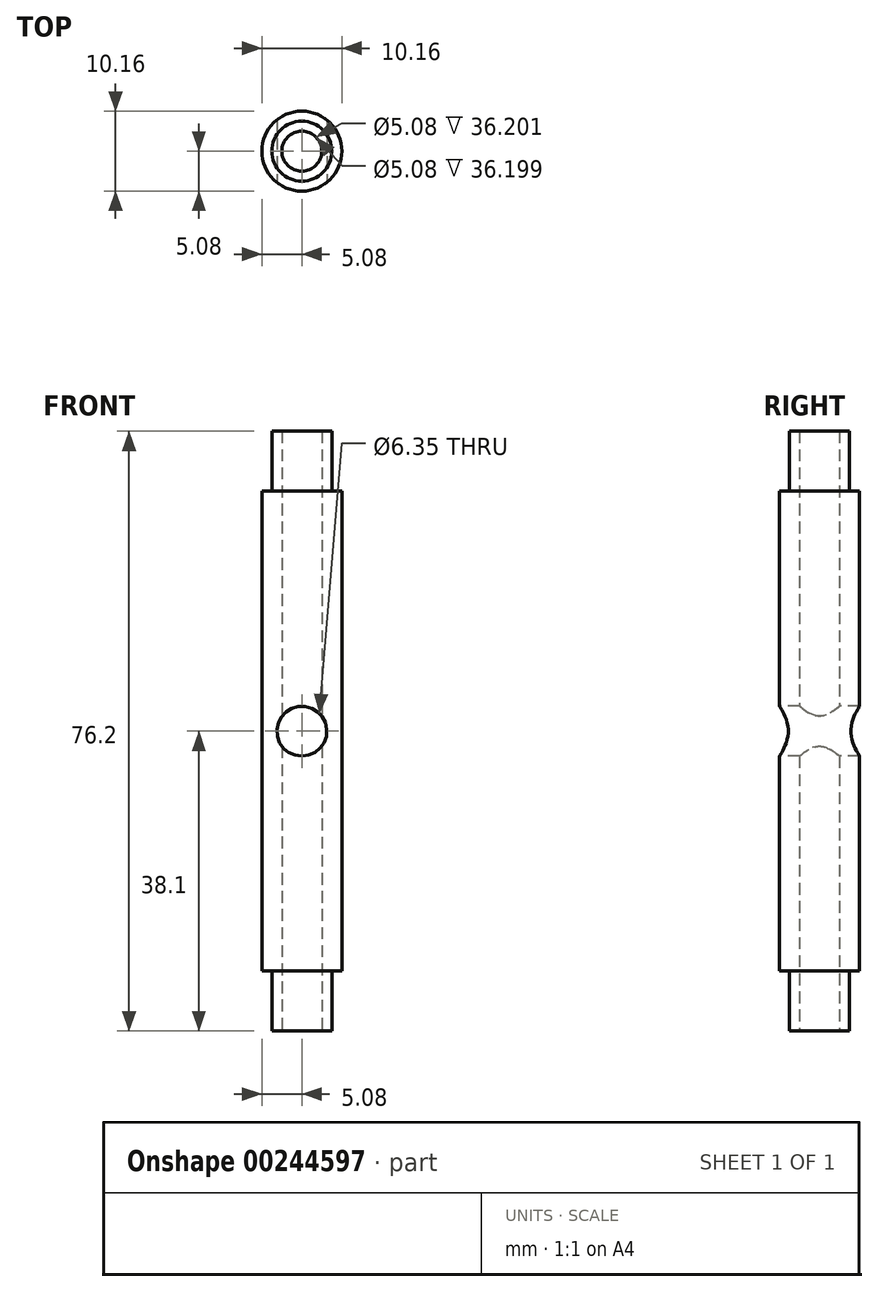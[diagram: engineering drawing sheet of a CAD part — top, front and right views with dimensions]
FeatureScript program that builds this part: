
annotation { "Feature Type Name" : "Feature", "Feature Type Description" : "" }
export const myFeature = defineFeature(function(context is Context, id is Id, definition is map)
    precondition{}
    {
        {
            var Q0;
            Q0=qCreatedBy(makeId("Top.planeOp"),FACE);
            var sketch = newSketch(context, id + "F0", { "sketchPlane" : qUnion([Q0])});
            skCircle(sketch, "E0", {"center": v(0, 0) * mm, "radius": 3.81 * mm});
            skSolve(sketch);
        }
        {
            var Q0;
            Q0 = qSketchRegion(id + "F0", true);
            extrude(context, id + "F1", {"entities" : qUnion([Q0]), "depth" : 7.62 * mm});
        }
        {
            var Q0;
            Q0=makeQuery(id+"F1.opExtrude","CAP_FACE",FACE,{"disambiguationData":[OSD([sQuery(id+"F0.wireOp",EDGE,"E0")])],"isStart":false});
            var sketch = newSketch(context, id + "F2", { "sketchPlane" : qUnion([Q0])});
            skCircle(sketch, "E1", {"center": v(0, 0) * mm, "radius": 5.08 * mm});
            skSolve(sketch);
        }
        {
            var Q0;
            Q0 = qSketchRegion(id + "F2", true);
            extrude(context, id + "F3", {"entities" : qUnion([Q0]), "operationType" : NewBodyOperationType.ADD, "depth" : 60.96 * mm});
        }
        {
            var Q0;
            Q0=makeQuery(id+"F3.opExtrude","CAP_FACE",FACE,{"disambiguationData":[OSD([sQuery(id+"F2.wireOp",EDGE,"E1")])],"isStart":false});
            var sketch = newSketch(context, id + "F4", { "sketchPlane" : qUnion([Q0])});
            skCircle(sketch, "E2", {"center": v(0, 0) * mm, "radius": 3.81 * mm});
            skSolve(sketch);
        }
        {
            var Q0;
            Q0 = qSketchRegion(id + "F4", true);
            extrude(context, id + "F5", {"entities" : qUnion([Q0]), "operationType" : NewBodyOperationType.ADD, "depth" : 7.62 * mm});
        }
        {
            var Q0;
            Q0=qCreatedBy(makeId("Front.planeOp"),FACE);
            var sketch = newSketch(context, id + "F6", { "sketchPlane" : qUnion([Q0])});
            skCircle(sketch, "E3", {"center": v(0, 38.1) * mm, "radius": 3.18 * mm});
            skSolve(sketch);
        }
        {
            var Q0;
            Q0 = qSketchRegion(id + "F6", true);
            extrude(context, id + "F7", {"entities" : qUnion([Q0]), "operationType" : NewBodyOperationType.REMOVE, "oppositeDirection" : true, "depth" : 25.4 * mm, "hasSecondDirection" : true, "secondDirectionOppositeDirection" : false, "secondDirectionDepth" : 25.4 * mm});
        }
        {
            var Q0;
            Q0=makeQuery(id+"F1.opExtrude","CAP_FACE",FACE,{"disambiguationData":[OSD([sQuery(id+"F0.wireOp",EDGE,"E0")])],"isStart":true});
            var sketch = newSketch(context, id + "F8", { "sketchPlane" : qUnion([Q0])});
            skCircle(sketch, "E4", {"center": v(0, 0) * mm, "radius": 2.54 * mm});
            skSolve(sketch);
        }
        {
            var Q0;
            Q0 = qSketchRegion(id + "F8", true);
            extrude(context, id + "F9", {"entities" : qUnion([Q0]), "operationType" : NewBodyOperationType.REMOVE, "endBound" : BoundingType.THROUGH_ALL, "oppositeDirection" : true, "depth" : 25.4 * mm});
        }
    });
